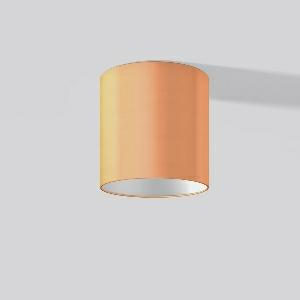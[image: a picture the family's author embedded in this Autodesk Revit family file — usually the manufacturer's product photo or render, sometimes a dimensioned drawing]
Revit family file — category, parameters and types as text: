
# Revit family: toledo_flatliner_901634_002_9799
name_source: partatom
category: Lighting Fixtures
units: mm (PartAtom-declared; Revit-internal decimal feet)

## family parameters
Cut with Voids When Loaded = No
Host = Face
Light Source = No
Part Type = Normal
Room Calculation Point = No
Round Connector Dimension = Use Diameter
Shared = No

## types (1)
- 982302.002 (1 x LED Modul 830, 1700 lm, 3000)
    Apparent Load = 22 VA
    CIE Flux Codes = 50 82 97 99 100
    Color Rendering = 80
    Color Temperature = 3000
    Default Elevation = 1800 mm
    Description = Series: TOLEDO FLATLINER
Decorative ceiling luminaire for interior decoration. Base luminaire prepared for the installation of fabric lampshade. Cylinder housing sheet steel, powder-coated. Housing: die cast aluminium and sheet steel, powder-coated. Bezel ring: die-cast aluminium, powder-coated. Lightguide and diffuser made of non-yellowing plastic (PMMA) opal matt. Modular design: With the basic luminaire, a square or cylindrical fabric lampshade must always be ordered separately. Fabric lampshades can be fitted to the basic luminaire without tools. Order satin finish diffuser as separate accessory. 
Colour: white
Diameter: 330 mm
Height: 70 mm
Lamp: LED
Socket: without socket
Colour temperature: 3000K
Colour rendering index (CRI): 80
System power: 22 W
Rated luminous flux: 1700 lm
Luminous efficiency: 77 lm/W
Control gear: Regulated power supply
Protection class: II
Type of protection: IP 40
    Height = 70 mm
    Lamp = 1 x LED Modul 830
    Lamp Light Flux = 1700 lm
    Lamp count = 1
    Length = 330 mm
    Lifetime = 50000 h
    Luminous efficacy = 77 lm/W
    Manufacturer = RZB
    ModVariant = No
    Model = 901634.002
    Mounting Place = Ceiling
    Mounting Type = Surface mounted
    Number of Poles = 1
    OnlyDefault = Yes
    Power Factor = 1
    Product Name = TOLEDO FLATLINER
    Product group = Surface mounted ceiling Fabric lampshade luminaires
    ProductGroupID = 313
    Protection Class = Protection class II
    Protection Degree = IP 40
    RLX_Detail_Level = 1
    RLX_Emergency_Light_Flux = 0 lm
    RLX_Emergency_Type = 0
    RLX_Emergency_Type_DB = No
    RlxData = <blob elided: 63037 chars, md5=a295e65f>
    Socket = socket
    Standby Power = 0 W
    System Light Flux = 1700 lm
    System Power = 22 W
    Type Image = toledo_flatliner_anbau_rund_orange_odeckel.jpg
    URL = http://relux.com
    VarID = 982302_002_891e
    Voltage = 230 V
    Voltage Range = 220-240 V
    Weight = 0.00 kg
    Width = 0 mm  [stored 0 ft]

note: [stored X ft] marks values corroborated as IEEE doubles in the binary element streams (Revit-internal decimal feet)

## geometry (parser evidence)
native form markers: Blend x4, Sweep x9
no freeform markers — native parametric forms only
